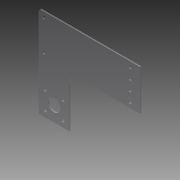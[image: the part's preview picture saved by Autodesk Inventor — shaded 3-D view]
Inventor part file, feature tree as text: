
AUTODESK INVENTOR PART (.ipt)
format: ipt  version: 2014 (Build 180170000, 170)  size: 114,688 bytes
history: native  units: in
note: dims shown in document units (in); Inventor stores cm internally (conversion verified against a paired STEP export)
features: extrude x1, sketch x1
ambient origin geometry x8: Origin, YZ Plane, XZ Plane, XY Plane, X Axis, Y Axis, Z Axis, Center Point
bodies: Solid1 (feature_tree)
feature tree (2):
  extrude  "Extrusion1"  Depth=5.0in
  sketch  "Sketch1"  dims[d0=4.5in d1=5.0in d3=0.0625in d4=0.0in d5=1.5in d7=0.625in d8=0.5in d9=0.75in d10=0.75in d11=0.5in d12=0.125in d13=0.164in d14=0.5in d15=0.25in d16=1.5748in d18=0.5in d19=0.3937in d21=1.0in d23=0.164in d25=0.625in d26=45.0deg d27=1.5748in d29=360.0deg d31=0.25in d32=0.25in d33=0.7874in d35=1.5in d36=0.3937in d38=1.0in d40=2.0in]
